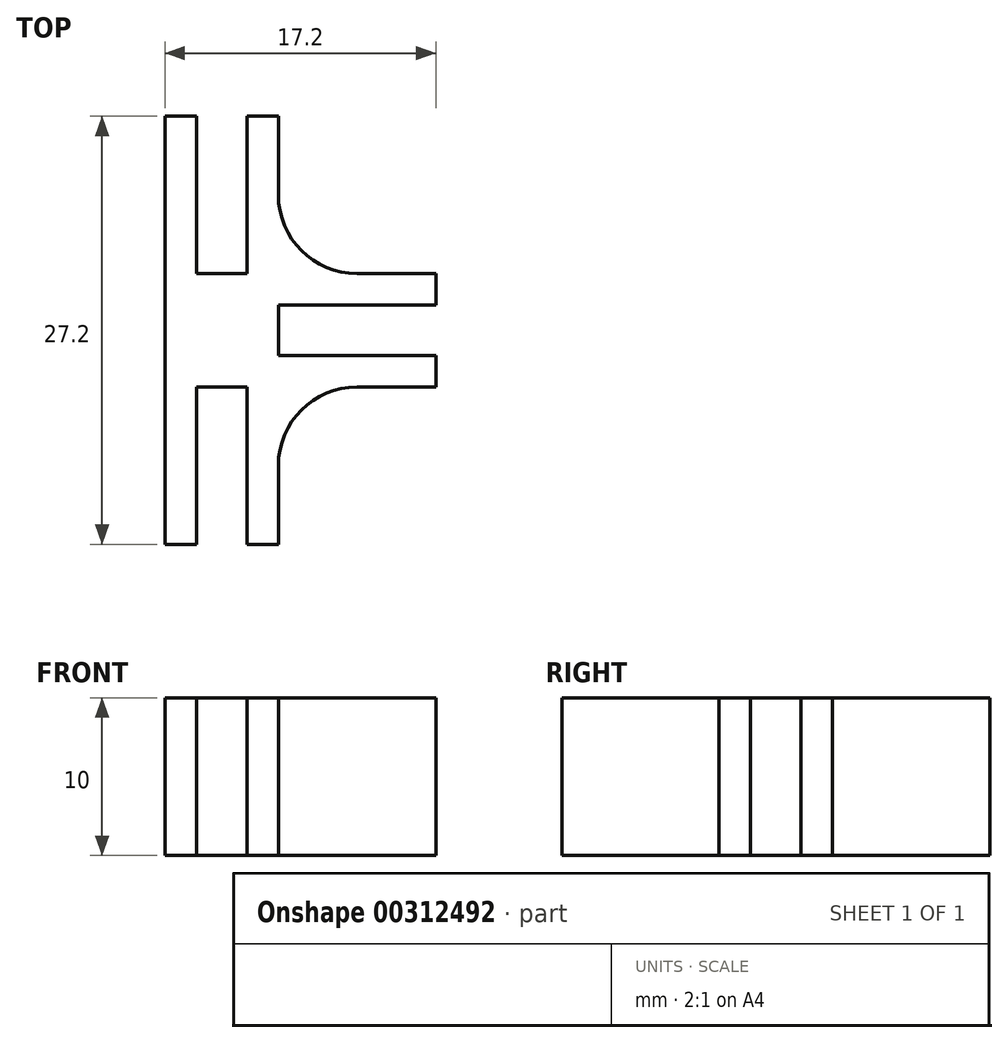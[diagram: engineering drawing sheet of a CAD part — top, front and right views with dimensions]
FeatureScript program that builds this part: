
annotation { "Feature Type Name" : "Feature", "Feature Type Description" : "" }
export const myFeature = defineFeature(function(context is Context, id is Id, definition is map)
    precondition{}
    {
        {
            assignVariable(context, id + "F0", {"name" : "h", "anyValue" : 10});
        }
        {
            var Q0;
            Q0=qCreatedBy(makeId("Top.planeOp"),FACE);
            var sketch = newSketch(context, id + "F1", { "sketchPlane" : qUnion([Q0])});
            skLineSegment(sketch, "E0", {"start": v(-2, 13.6) * mm, "end": v(-2, 3.6) * mm});
            skLineSegment(sketch, "E1", {"start": v(-2, 3.6) * mm, "end": v(-5.2, 3.6) * mm});
            skLineSegment(sketch, "E2", {"start": v(-5.2, 3.6) * mm, "end": v(-5.2, 13.6) * mm});
            skLineSegment(sketch, "E3", {"start": v(-5.2, 13.6) * mm, "end": v(-7.2, 13.6) * mm});
            skLineSegment(sketch, "E4", {"start": v(-7.2, 13.6) * mm, "end": v(-7.2, -3.6) * mm});
            skLineSegment(sketch, "E5", {"start": v(0, -3.6) * mm, "end": v(10, -3.6) * mm});
            skLineSegment(sketch, "E6", {"start": v(10, -3.6) * mm, "end": v(10, -1.6) * mm});
            skLineSegment(sketch, "E7", {"start": v(10, -1.6) * mm, "end": v(0, -1.6) * mm});
            skLineSegment(sketch, "E8", {"start": v(0, -1.6) * mm, "end": v(0, 1.6) * mm});
            skLineSegment(sketch, "E9", {"start": v(0, 1.6) * mm, "end": v(10, 1.6) * mm});
            skLineSegment(sketch, "E10", {"start": v(10, 1.6) * mm, "end": v(10, 3.6) * mm});
            skLineSegment(sketch, "E11", {"start": v(10, 3.6) * mm, "end": v(0, 3.6) * mm});
            skLineSegment(sketch, "E12", {"start": v(0, 3.6) * mm, "end": v(0, 13.6) * mm});
            skLineSegment(sketch, "E13", {"start": v(0, 13.6) * mm, "end": v(-2, 13.6) * mm});
            skLineSegment(sketch, "E14", {"start": v(-2, 3.6) * mm, "end": v(0, 3.6) * mm, "construction": true});
            skLineSegment(sketch, "E15", {"start": v(0, 1.6) * mm, "end": v(0, 3.6) * mm, "construction": true});
            skPoint(sketch, "E16", {"position": v(0, 0) * mm});
            skLineSegment(sketch, "E17.MirrorCS", {"start": v(-7.2, -13.6) * mm, "end": v(-7.2, 3.6) * mm});
            skLineSegment(sketch, "E18.MirrorCS", {"start": v(-5.2, -3.6) * mm, "end": v(-5.2, -13.6) * mm});
            skLineSegment(sketch, "E19.MirrorCS", {"start": v(-5.2, -13.6) * mm, "end": v(-7.2, -13.6) * mm});
            skLineSegment(sketch, "E20.MirrorCS", {"start": v(-2, -13.6) * mm, "end": v(-2, -3.6) * mm});
            skLineSegment(sketch, "E21.MirrorCS", {"start": v(0, -13.6) * mm, "end": v(-2, -13.6) * mm});
            skLineSegment(sketch, "E22.MirrorCS", {"start": v(-2, -3.6) * mm, "end": v(-5.2, -3.6) * mm});
            skLineSegment(sketch, "E23.MirrorCS", {"start": v(0, -3.6) * mm, "end": v(0, -13.6) * mm});
            skSolve(sketch);
        }
        {
            var Q0;
            Q0=makeQuery(id+"F1.imprint","IMPRINT",FACE,{"disambiguationData":[TD([[makeQuery(id+"F1.imprint","IMPRINT",EDGE,{"derivedFrom":sQuery(id+"F1.wireOp",EDGE,"E0")}),1.0]])]});
            extrude(context, id + "F2", {"entities" : qUnion([Q0]), "depth" : (getVariable(context, 'h')) * mm});
        }
        {
            var Q0;
            Q0=makeQuery(id+"F2.opExtrude","SWEPT_EDGE",EDGE,{"disambiguationData":[OSD([sQuery(id+"F1.wireOp",EDGE,"E5"),sQuery(id+"F1.wireOp",EDGE,"E23.MirrorCS")])]});
            var Q1;
            Q1=makeQuery(id+"F2.opExtrude","SWEPT_EDGE",EDGE,{"disambiguationData":[OSD([sQuery(id+"F1.wireOp",EDGE,"E11"),sQuery(id+"F1.wireOp",EDGE,"E12")])]});
            fillet(context, id + "F3", {"entities" : qUnion([Q0, Q1]), "radius" : 5 * mm, "tangentPropagation" : true, "allowEdgeOverflow" : false});
        }
    });
